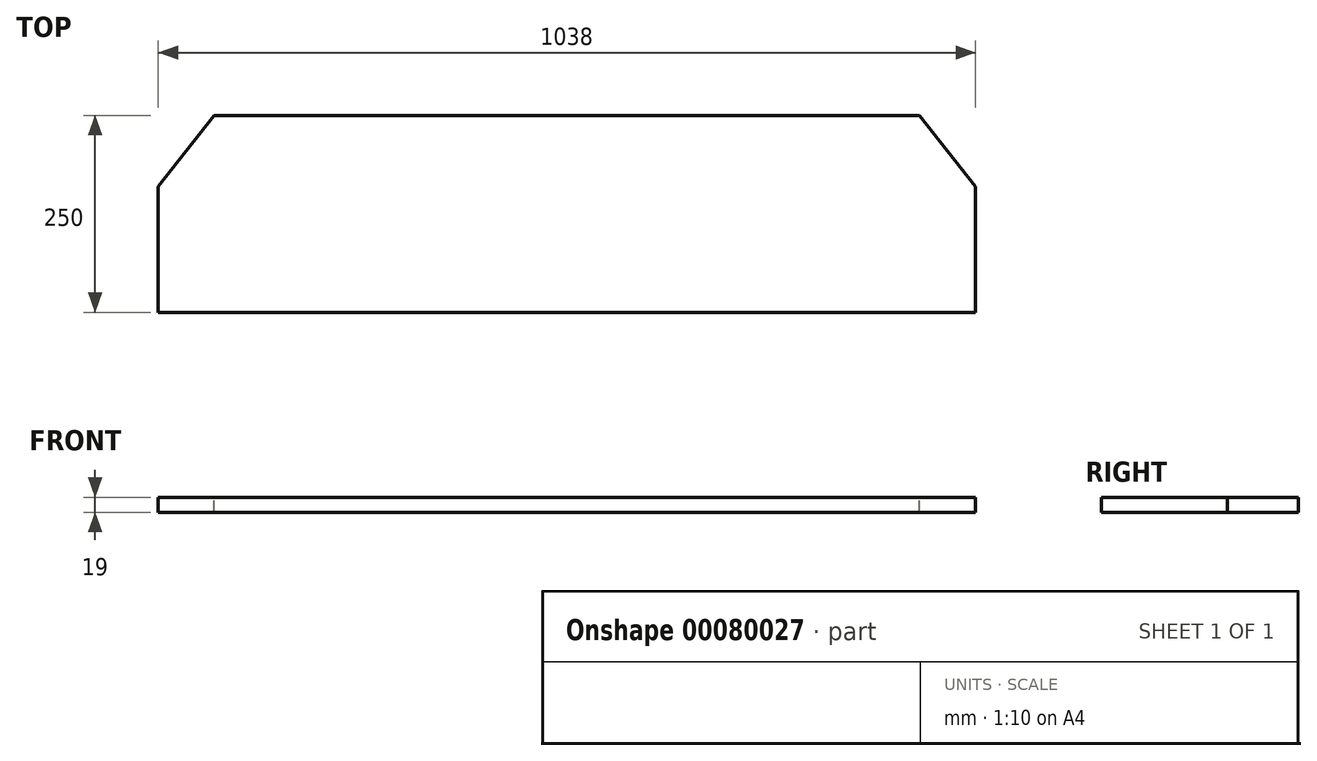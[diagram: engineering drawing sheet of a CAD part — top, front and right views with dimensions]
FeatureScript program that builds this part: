
annotation { "Feature Type Name" : "Feature", "Feature Type Description" : "" }
export const myFeature = defineFeature(function(context is Context, id is Id, definition is map)
    precondition{}
    {
        {
            var Q0;
            Q0=qCreatedBy(makeId("Top.planeOp"),FACE);
            var sketch = newSketch(context, id + "F0", { "sketchPlane" : qUnion([Q0])});
            skLineSegment(sketch, "E0.bottom", {"start": v(0, 0) * mm, "end": v(1038, 0) * mm});
            skLineSegment(sketch, "E0.top", {"start": v(0, -250) * mm, "end": v(1038, -250) * mm});
            skLineSegment(sketch, "E0.left", {"start": v(0, 0) * mm, "end": v(0, -250) * mm});
            skLineSegment(sketch, "E0.right", {"start": v(1038, 0) * mm, "end": v(1038, -250) * mm});
            skSolve(sketch);
        }
        {
            var Q0;
            Q0 = qSketchRegion(id + "F0", true);
            extrude(context, id + "F1", {"entities" : qUnion([Q0]), "depth" : 19 * mm});
        }
        {
            var Q0;
            Q0=makeQuery(id+"F1.opExtrude","CAP_FACE",FACE,{"disambiguationData":[OSD([sQuery(id+"F0.wireOp",EDGE,"E0.bottom"),sQuery(id+"F0.wireOp",EDGE,"E0.top"),sQuery(id+"F0.wireOp",EDGE,"E0.left"),sQuery(id+"F0.wireOp",EDGE,"E0.right")])],"isStart":false});
            var sketch = newSketch(context, id + "F2", { "sketchPlane" : qUnion([Q0])});
            skLineSegment(sketch, "E1", {"start": v(0, -90) * mm, "end": v(71.23, 0) * mm});
            skLineSegment(sketch, "E2", {"start": v(966.77, 0) * mm, "end": v(1038, -90) * mm});
            skSolve(sketch);
        }
        {
            var Q0;
            {var subQ0=sQuery(id+"F2.wireOp",EDGE,"E2");Q0=makeQuery(id+"F2.imprint","IMPRINT",FACE,{"disambiguationData":[TD([[makeQuery(id+"F2.imprint","IMPRINT",EDGE,{"derivedFrom":subQ0}),1.0]])]});}
            var Q1;
            {var subQ0=sQuery(id+"F2.wireOp",EDGE,"E1");Q1=makeQuery(id+"F2.imprint","IMPRINT",FACE,{"disambiguationData":[TD([[makeQuery(id+"F2.imprint","IMPRINT",EDGE,{"derivedFrom":subQ0}),1.0]])]});}
            extrude(context, id + "F3", {"entities" : qUnion([Q0, Q1]), "operationType" : NewBodyOperationType.REMOVE, "oppositeDirection" : true, "depth" : 19 * mm});
        }
    });
